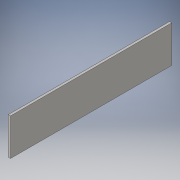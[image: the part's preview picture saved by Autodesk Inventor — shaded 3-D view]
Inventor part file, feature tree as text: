
AUTODESK INVENTOR PART (.ipt)
format: ipt  version: 2016 (Build 200138000, 138)  size: 93,184 bytes
history: native  units: in
note: dims shown in document units (in); Inventor stores cm internally (conversion verified against a paired STEP export)
features: sketch x2, extrude x1
ambient origin geometry x8: Origin, YZ Plane, XZ Plane, XY Plane, X Axis, Y Axis, Z Axis, Center Point
bodies: Solid1 (feature_tree)
feature tree (3):
  extrude  "Extrusion1"  Depth=17.5in
  sketch  "Sketch2"  dims[d4=2.0in d5=1.5in d6=2.0in d7=1.5in d8=0.25in d9=0.0in]
  sketch  "Sketch1"  dims[d2=4.0in d3=17.5in]
